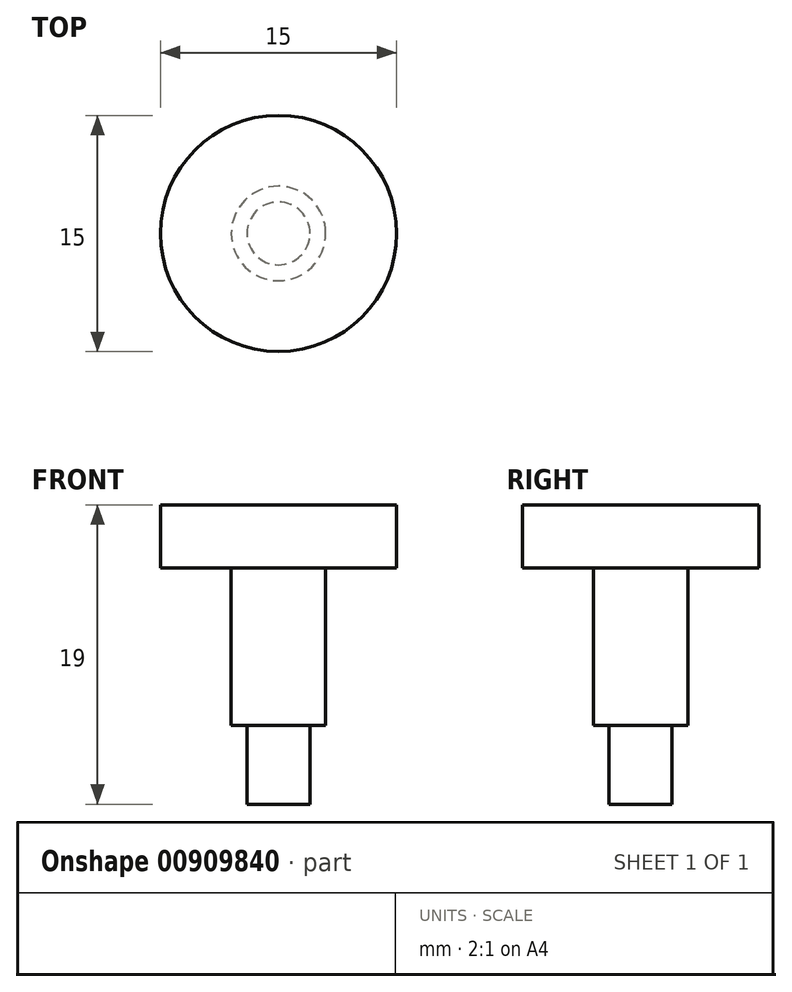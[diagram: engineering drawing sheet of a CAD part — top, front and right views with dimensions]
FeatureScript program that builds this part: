
annotation { "Feature Type Name" : "Feature", "Feature Type Description" : "" }
export const myFeature = defineFeature(function(context is Context, id is Id, definition is map)
    precondition{}
    {
        {
            var Q0;
            Q0=qCreatedBy(makeId("Front.planeOp"),FACE);
            var sketch = newSketch(context, id + "F0", { "sketchPlane" : qUnion([Q0])});
            skLineSegment(sketch, "E0", {"start": v(0, 0) * mm, "end": v(2, 0) * mm});
            skLineSegment(sketch, "E1", {"start": v(2, 0) * mm, "end": v(2, 5) * mm});
            skLineSegment(sketch, "E2", {"start": v(2, 5) * mm, "end": v(3, 5) * mm});
            skLineSegment(sketch, "E3", {"start": v(3, 5) * mm, "end": v(3, 15) * mm});
            skLineSegment(sketch, "E4", {"start": v(3, 15) * mm, "end": v(7.5, 15) * mm});
            skLineSegment(sketch, "E5", {"start": v(7.5, 15) * mm, "end": v(7.5, 19) * mm});
            skLineSegment(sketch, "E6", {"start": v(7.5, 19) * mm, "end": v(0, 19) * mm});
            skLineSegment(sketch, "E7", {"start": v(0, -6.48) * mm, "end": v(0, 24.12) * mm, "construction": true});
            skLineSegment(sketch, "E8", {"start": v(0, 19) * mm, "end": v(0, 0) * mm});
            skSolve(sketch);
        }
        {
            var Q0;
            Q0=qSketchRegion(id+"F0",true);
            var Q1;
            Q1=sQuery(id+"F0.wireOp",EDGE,"E7");
            revolve(context, id + "F1", {"surfaceOperationType" : NewSurfaceOperationType.NEW, "entities" : qUnion([Q0]), "axis" : qUnion([Q1]), "revolveType" : RevolveType.FULL});
        }
    });
